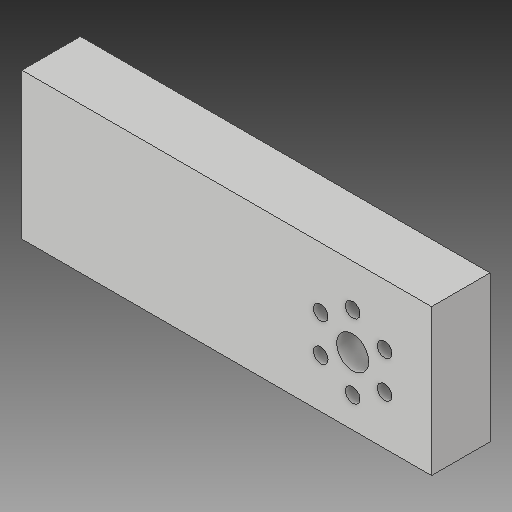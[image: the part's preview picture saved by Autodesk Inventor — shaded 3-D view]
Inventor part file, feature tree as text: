
AUTODESK INVENTOR PART (.ipt)
format: ipt  version: 2019 (Build 230136000, 136)  size: 134,656 bytes
history: native  units: in
note: dims shown in document units (in); Inventor stores cm internally (conversion verified against a paired STEP export)
features: sketch x3, extrude x2, thicken_offset x1, hole x1
ambient origin geometry x8: Origin, YZ Plane, XZ Plane, XY Plane, X Axis, Y Axis, Z Axis, Center Point
bodies: Solid1 (feature_tree)
feature tree (7):
  extrude  "Extrusion1"  Depth=1.25in
  extrude  "Extrusion2"  Depth=0.5in
  thicken_offset  "Thicken1"
  hole  "Hole1"  [1 undecoded]
  sketch  "Sketch1"  dims[d0=2.5in d1=1.25in]
  sketch  "Sketch2"  dims[d2=0.5in d3=0.0in d6=0.575in]
  sketch  "Sketch4"  dims[d7=90.0deg d8=0.275in d9=0.63in d10=0.125in d11=2.3622in d13=360.0deg d15=0.75in d16=0.0in d17=0.674in d28=1.0in d29=1.0in d35=0.13in d36=0.25in d37=0.375in d38=0.25in d39=0.5635in d40=0.3in d41=0.8108in d42=0.25in d43=3.5in d44=1.75in d45=0.25in]
note: 1 required parameter value undecoded (feature->parameter linkage not recoverable at this tier; creation-order binding heuristic only, values carry confidence <= 0.55)
